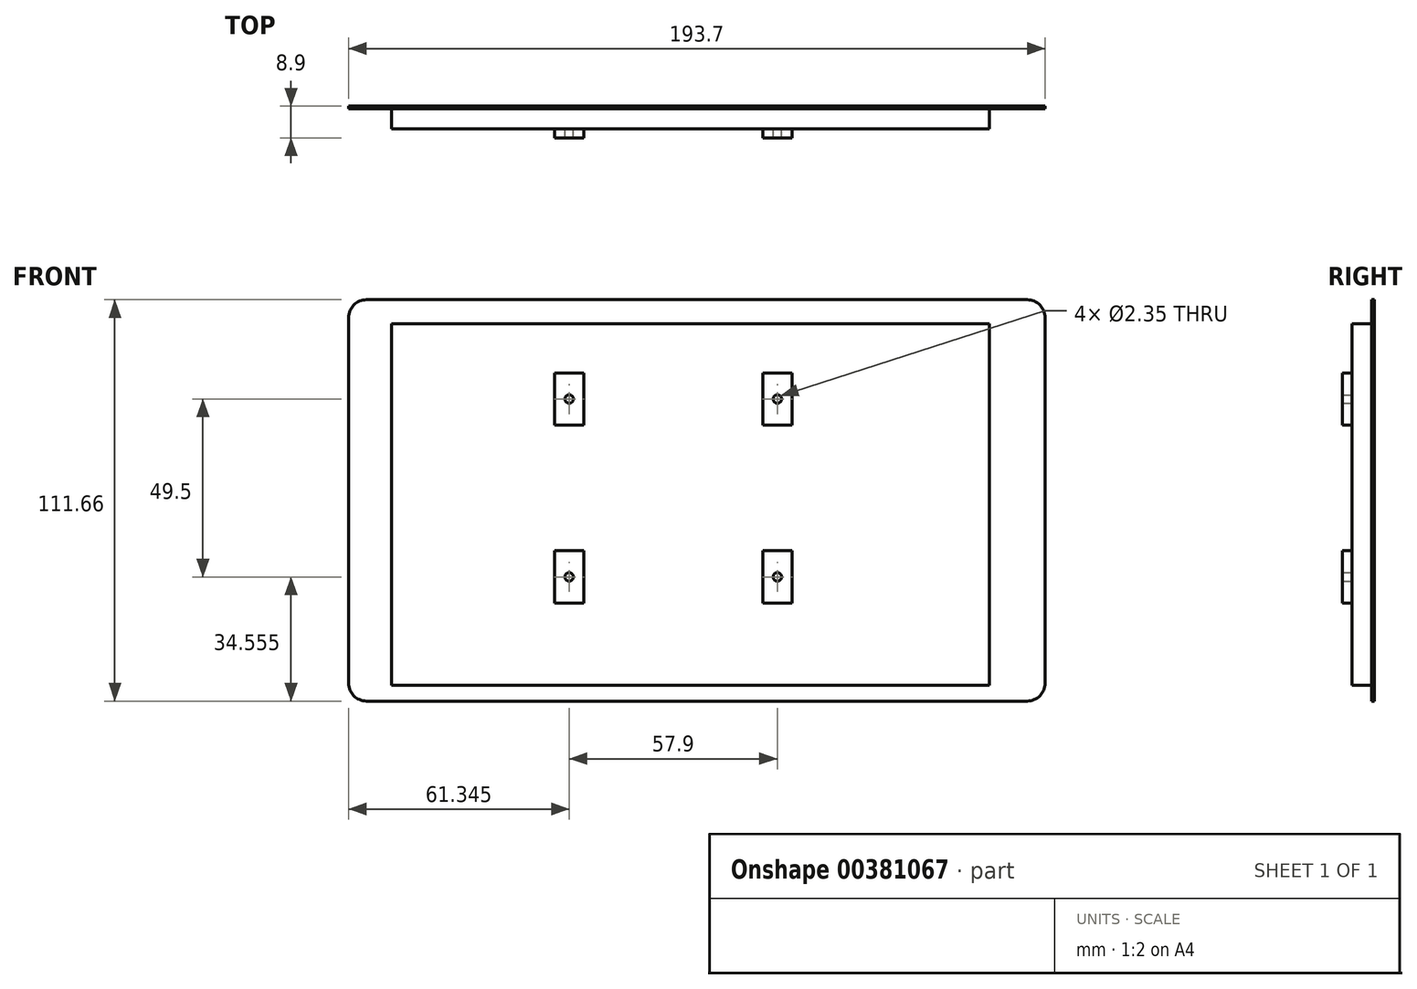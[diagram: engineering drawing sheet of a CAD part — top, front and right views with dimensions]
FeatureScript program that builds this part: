
annotation { "Feature Type Name" : "Feature", "Feature Type Description" : "" }
export const myFeature = defineFeature(function(context is Context, id is Id, definition is map)
    precondition{}
    {
        {
            var Q0;
            Q0=qCreatedBy(makeId("Front.planeOp"),FACE);
            var sketch = newSketch(context, id + "F0", { "sketchPlane" : qUnion([Q0])});
            skLineSegment(sketch, "E0", {"start": v(0, 0) * mm, "end": v(98.58, 0) * mm, "construction": true});
            skLineSegment(sketch, "E1", {"start": v(0, 0) * mm, "end": v(-95.12, 0) * mm, "construction": true});
            skLineSegment(sketch, "E2", {"start": v(-95.12, 0) * mm, "end": v(-95.12, 51.98) * mm});
            skLineSegment(sketch, "E3", {"start": v(-95.12, 0) * mm, "end": v(-95.12, -49.68) * mm});
            skLineSegment(sketch, "E4", {"start": v(98.58, 0) * mm, "end": v(98.58, 51.98) * mm});
            skLineSegment(sketch, "E5", {"start": v(98.58, 0) * mm, "end": v(98.58, -49.68) * mm});
            skLineSegment(sketch, "E6", {"start": v(93.58, -54.68) * mm, "end": v(-90.12, -54.68) * mm});
            skLineSegment(sketch, "E7", {"start": v(-90.12, 56.97) * mm, "end": v(93.58, 56.97) * mm});
            skPoint(sketch, "E8.visualSharp", {"position": v(-95.12, 56.97) * mm});
            skArc(sketch, "E8.filletArc", {"start": v(-90.12, 56.97) * mm, "mid": v(-93.66, 55.51) * mm, "end": v(-95.12, 51.98) * mm});
            skPoint(sketch, "E9.visualSharp", {"position": v(98.58, 56.98) * mm});
            skArc(sketch, "E9.filletArc", {"start": v(98.58, 51.98) * mm, "mid": v(97.11, 55.51) * mm, "end": v(93.58, 56.97) * mm});
            skPoint(sketch, "E10.visualSharp", {"position": v(98.58, -54.68) * mm});
            skArc(sketch, "E10.filletArc", {"start": v(93.58, -54.68) * mm, "mid": v(97.11, -53.21) * mm, "end": v(98.58, -49.68) * mm});
            skPoint(sketch, "E11.visualSharp", {"position": v(-95.12, -54.68) * mm});
            skArc(sketch, "E11.filletArc", {"start": v(-95.12, -49.68) * mm, "mid": v(-93.66, -53.21) * mm, "end": v(-90.12, -54.68) * mm});
            skSolve(sketch);
        }
        {
            var Q0;
            Q0 = qSketchRegion(id + "F0", true);
            extrude(context, id + "F1", {"entities" : qUnion([Q0]), "depth" : 0.8 * mm});
        }
        {
            var Q0;
            Q0=makeQuery(id+"F1.opExtrude","CAP_FACE",FACE,{"disambiguationData":[OSD([sQuery(id+"F0.wireOp",EDGE,"E2"),sQuery(id+"F0.wireOp",EDGE,"E3"),sQuery(id+"F0.wireOp",EDGE,"E4"),sQuery(id+"F0.wireOp",EDGE,"E5"),sQuery(id+"F0.wireOp",EDGE,"E6"),sQuery(id+"F0.wireOp",EDGE,"E7"),sQuery(id+"F0.wireOp",EDGE,"E8.filletArc"),sQuery(id+"F0.wireOp",EDGE,"E9.filletArc"),sQuery(id+"F0.wireOp",EDGE,"E10.filletArc"),sQuery(id+"F0.wireOp",EDGE,"E11.filletArc")])],"isStart":false});
            var sketch = newSketch(context, id + "F2", { "sketchPlane" : qUnion([Q0])});
            skLineSegment(sketch, "E12.bottom", {"start": v(83.12, 50.33) * mm, "end": v(-83.12, 50.33) * mm});
            skLineSegment(sketch, "E12.top", {"start": v(83.13, -50.33) * mm, "end": v(-83.12, -50.33) * mm});
            skLineSegment(sketch, "E12.left", {"start": v(83.13, 50.33) * mm, "end": v(83.13, -50.33) * mm});
            skLineSegment(sketch, "E12.right", {"start": v(-83.13, 50.33) * mm, "end": v(-83.12, -50.33) * mm});
            skPoint(sketch, "E12.middle", {"position": v(0, 0) * mm});
            skSolve(sketch);
        }
        {
            var Q0;
            Q0=makeQuery(id+"F2.imprint","IMPRINT",FACE,{"disambiguationData":[TD([[makeQuery(id+"F2.imprint","IMPRINT",EDGE,{"derivedFrom":sQuery(id+"F2.wireOp",EDGE,"E12.bottom")}),1.0]])]});
            extrude(context, id + "F3", {"entities" : qUnion([Q0]), "operationType" : NewBodyOperationType.ADD, "depth" : 5.5 * mm});
        }
        {
            var Q0;
            Q0=makeQuery(id+"F3.opExtrude","CAP_FACE",FACE,{"disambiguationData":[OSD([sQuery(id+"F2.wireOp",EDGE,"E12.bottom"),sQuery(id+"F2.wireOp",EDGE,"E12.top"),sQuery(id+"F2.wireOp",EDGE,"E12.left"),sQuery(id+"F2.wireOp",EDGE,"E12.right")])],"isStart":false});
            var sketch = newSketch(context, id + "F4", { "sketchPlane" : qUnion([Q0])});
            skLineSegment(sketch, "E13", {"start": v(-83.12, 36.63) * mm, "end": v(-37.83, 36.63) * mm, "construction": true});
            skLineSegment(sketch, "E14", {"start": v(-37.83, 36.63) * mm, "end": v(-37.83, 50.33) * mm, "construction": true});
            skLineSegment(sketch, "E15.bottom", {"start": v(-37.83, 36.63) * mm, "end": v(-29.73, 36.63) * mm});
            skLineSegment(sketch, "E15.top", {"start": v(-37.83, 22.13) * mm, "end": v(-29.73, 22.13) * mm});
            skLineSegment(sketch, "E15.left", {"start": v(-37.83, 36.63) * mm, "end": v(-37.83, 22.13) * mm});
            skLineSegment(sketch, "E15.right", {"start": v(-29.73, 36.63) * mm, "end": v(-29.73, 22.13) * mm});
            skLineSegment(sketch, "E16", {"start": v(-37.83, 36.63) * mm, "end": v(28.18, 36.63) * mm, "construction": true});
            skPoint(sketch, "E16.endSnap0", {"position": v(-33.78, 36.63) * mm});
            skLineSegment(sketch, "E17.bottom", {"start": v(28.18, 36.63) * mm, "end": v(20.08, 36.63) * mm});
            skLineSegment(sketch, "E17.top", {"start": v(28.18, 22.13) * mm, "end": v(20.08, 22.13) * mm});
            skLineSegment(sketch, "E17.left", {"start": v(28.18, 36.63) * mm, "end": v(28.18, 22.13) * mm});
            skLineSegment(sketch, "E17.right", {"start": v(20.08, 36.63) * mm, "end": v(20.08, 22.13) * mm});
            skLineSegment(sketch, "E18.bottom", {"start": v(28.18, -27.37) * mm, "end": v(20.08, -27.37) * mm});
            skLineSegment(sketch, "E18.top", {"start": v(28.18, -12.87) * mm, "end": v(20.08, -12.87) * mm});
            skLineSegment(sketch, "E18.left", {"start": v(28.18, -27.37) * mm, "end": v(28.18, -12.87) * mm});
            skLineSegment(sketch, "E18.right", {"start": v(20.08, -27.37) * mm, "end": v(20.08, -12.87) * mm});
            skLineSegment(sketch, "E19", {"start": v(28.18, -27.37) * mm, "end": v(-37.82, -27.37) * mm, "construction": true});
            skLineSegment(sketch, "E20.bottom", {"start": v(-37.82, -27.37) * mm, "end": v(-29.72, -27.37) * mm});
            skLineSegment(sketch, "E20.top", {"start": v(-37.82, -12.87) * mm, "end": v(-29.72, -12.87) * mm});
            skLineSegment(sketch, "E20.left", {"start": v(-37.82, -27.37) * mm, "end": v(-37.82, -12.87) * mm});
            skLineSegment(sketch, "E20.right", {"start": v(-29.72, -27.37) * mm, "end": v(-29.72, -12.87) * mm});
            skLineSegment(sketch, "E21", {"start": v(28.18, 36.63) * mm, "end": v(28.18, -27.37) * mm, "construction": true});
            skCircle(sketch, "E22", {"center": v(-33.78, 29.38) * mm, "radius": 1.18 * mm});
            skPoint(sketch, "E22.centerSnap0", {"position": v(-29.73, 29.38) * mm});
            skCircle(sketch, "E23", {"center": v(24.13, 29.38) * mm, "radius": 1.18 * mm});
            skPoint(sketch, "E23.centerSnap0", {"position": v(28.18, 29.38) * mm});
            skPoint(sketch, "E23.centerSnap1", {"position": v(24.13, 22.13) * mm});
            skCircle(sketch, "E24", {"center": v(-33.78, -20.12) * mm, "radius": 1.18 * mm});
            skPoint(sketch, "E24.centerSnap0", {"position": v(-37.82, -20.12) * mm});
            skCircle(sketch, "E25", {"center": v(24.13, -20.12) * mm, "radius": 1.18 * mm});
            skPoint(sketch, "E25.centerSnap0", {"position": v(24.13, -12.87) * mm});
            skPoint(sketch, "E25.centerSnap1", {"position": v(20.08, -20.12) * mm});
            skSolve(sketch);
        }
        {
            var Q0;
            Q0=makeQuery(id+"F4.imprint","IMPRINT",FACE,{"disambiguationData":[TD([[makeQuery(id+"F4.imprint","IMPRINT",EDGE,{"derivedFrom":sQuery(id+"F4.wireOp",EDGE,"E15.bottom")}),-1.0]])]});
            var Q1;
            Q1=makeQuery(id+"F4.imprint","IMPRINT",FACE,{"disambiguationData":[TD([[makeQuery(id+"F4.imprint","IMPRINT",EDGE,{"derivedFrom":sQuery(id+"F4.wireOp",EDGE,"E17.bottom")}),1.0]])]});
            var Q2;
            Q2=makeQuery(id+"F4.imprint","IMPRINT",FACE,{"disambiguationData":[TD([[makeQuery(id+"F4.imprint","IMPRINT",EDGE,{"derivedFrom":sQuery(id+"F4.wireOp",EDGE,"E18.bottom")}),-1.0]])]});
            var Q3;
            Q3=makeQuery(id+"F4.imprint","IMPRINT",FACE,{"disambiguationData":[TD([[makeQuery(id+"F4.imprint","IMPRINT",EDGE,{"derivedFrom":sQuery(id+"F4.wireOp",EDGE,"E20.bottom")}),1.0]])]});
            var Q4;
            Q4=sQuery(id+"F4.wireOp",EDGE,"E21");
            var Q5;
            Q5=sQuery(id+"F4.wireOp",EDGE,"E20.left");
            var Q6;
            Q6=sQuery(id+"F4.wireOp",EDGE,"E20.top");
            var Q7;
            Q7=sQuery(id+"F4.wireOp",EDGE,"E18.bottom");
            var Q8;
            Q8=sQuery(id+"F4.wireOp",EDGE,"E20.bottom");
            var Q9;
            Q9=sQuery(id+"F4.wireOp",EDGE,"E18.right");
            var Q10;
            Q10=sQuery(id+"F4.wireOp",EDGE,"E18.top");
            var Q11;
            Q11=sQuery(id+"F4.wireOp",EDGE,"E18.left");
            var Q12;
            Q12=sQuery(id+"F4.wireOp",EDGE,"E17.right");
            var Q13;
            Q13=sQuery(id+"F4.wireOp",EDGE,"E15.top");
            var Q14;
            Q14=sQuery(id+"F4.wireOp",EDGE,"E15.left");
            var Q15;
            Q15=sQuery(id+"F4.wireOp",EDGE,"E17.left");
            var Q16;
            Q16=sQuery(id+"F4.wireOp",EDGE,"E17.top");
            var Q17;
            Q17=sQuery(id+"F4.wireOp",EDGE,"E17.bottom");
            var Q18;
            Q18=sQuery(id+"F4.wireOp",EDGE,"E15.right");
            var Q19;
            Q19=sQuery(id+"F4.wireOp",EDGE,"E20.right");
            var Q20;
            Q20=sQuery(id+"F4.wireOp",EDGE,"E15.bottom");
            extrude(context, id + "F5", {"entities" : qUnion([Q0, Q1, Q2, Q3]), "surfaceEntities" : qUnion([Q4, Q5, Q6, Q7, Q8, Q9, Q10, Q11, Q12, Q13, Q14, Q15, Q16, Q17, Q18, Q19, Q20]), "depth" : 2.6 * mm});
        }
    });
